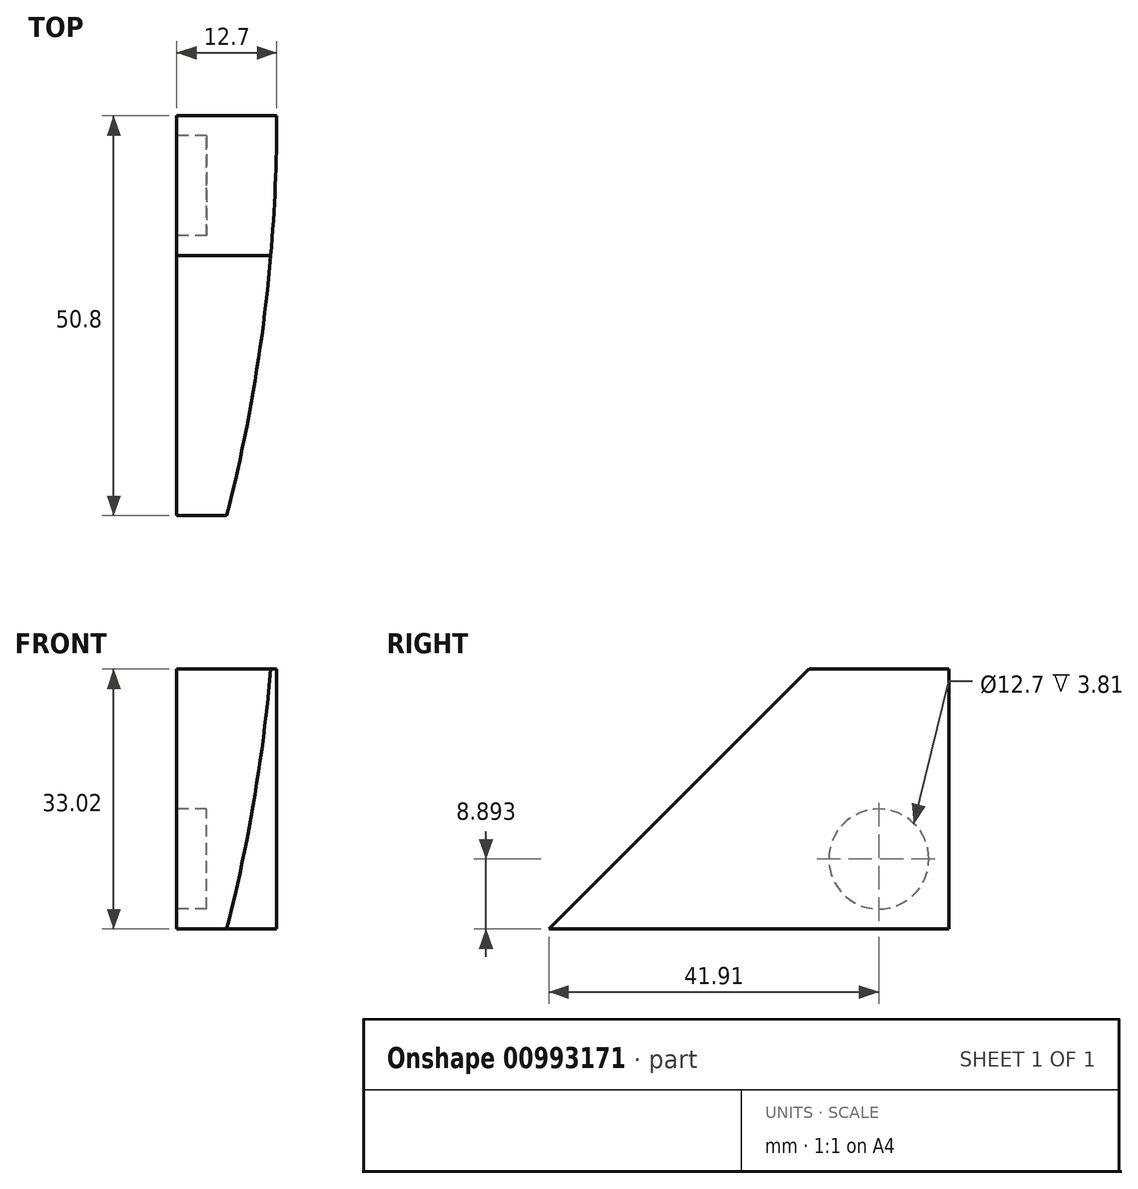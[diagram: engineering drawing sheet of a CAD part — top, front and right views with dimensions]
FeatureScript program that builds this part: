
annotation { "Feature Type Name" : "Feature", "Feature Type Description" : "" }
export const myFeature = defineFeature(function(context is Context, id is Id, definition is map)
    precondition{}
    {
        {
            var Q0;
            Q0=qCreatedBy(makeId("Right.planeOp"),FACE);
            var sketch = newSketch(context, id + "F0", { "sketchPlane" : qUnion([Q0])});
            skCircle(sketch, "E0", {"center": v(-28.5, 29.87) * mm, "radius": 6.35 * mm});
            skLineSegment(sketch, "E1.top", {"start": v(-70.4, 20.98) * mm, "end": v(-19.6, 20.98) * mm});
            skLineSegment(sketch, "E1.right", {"start": v(-19.6, 54) * mm, "end": v(-19.6, 20.98) * mm});
            skLineSegment(sketch, "E2", {"start": v(-70.4, 20.98) * mm, "end": v(-37.38, 54) * mm});
            skLineSegment(sketch, "E3", {"start": v(-37.38, 54) * mm, "end": v(-19.6, 54) * mm});
            skSolve(sketch);
        }
        {
            var Q0;
            Q0=makeQuery(id+"F0.imprint","IMPRINT",FACE,{"disambiguationData":[TD([[makeQuery(id+"F0.imprint","IMPRINT",EDGE,{"derivedFrom":sQuery(id+"F0.wireOp",EDGE,"E0")}),-1.0]])]});
            var Q1;
            Q1=makeQuery(id+"F0.imprint","IMPRINT",FACE,{"disambiguationData":[TD([[makeQuery(id+"F0.imprint","IMPRINT",EDGE,{"derivedFrom":sQuery(id+"F0.wireOp",EDGE,"E0")}),1.0]])]});
            extrude(context, id + "F1", {"entities" : qUnion([Q0, Q1]), "depth" : 12.7 * mm, "offsetDistance" : 25.4 * mm});
        }
        {
            var Q0;
            Q0=makeQuery(id+"F0.imprint","IMPRINT",FACE,{"disambiguationData":[TD([[makeQuery(id+"F0.imprint","IMPRINT",EDGE,{"derivedFrom":sQuery(id+"F0.wireOp",EDGE,"E0")}),1.0]])]});
            extrude(context, id + "F2", {"entities" : qUnion([Q0]), "operationType" : NewBodyOperationType.REMOVE, "depth" : 3.8 * mm, "offsetDistance" : 25.4 * mm});
        }
        {
            var Q0;
            Q0=makeQuery(id+"F1.opExtrude","SWEPT_FACE",FACE,{"disambiguationData":[OSD([sQuery(id+"F0.wireOp",EDGE,"E1.top")])]});
            var sketch = newSketch(context, id + "F3", { "sketchPlane" : qUnion([Q0])});
            skArc(sketch, "E4", {"start": v(12.7, 19.6) * mm, "mid": v(11.1, 45.2) * mm, "end": v(6.35, 70.4) * mm});
            skSolve(sketch);
        }
        {
            var Q0;
            {var subQ0=sQuery(id+"F3.wireOp",EDGE,"E4");Q0=makeQuery(id+"F3.imprint","IMPRINT",FACE,{"disambiguationData":[TD([[makeQuery(id+"F3.imprint","IMPRINT",EDGE,{"derivedFrom":subQ0}),-1.0]])]});}
            extrude(context, id + "F4", {"entities" : qUnion([Q0]), "operationType" : NewBodyOperationType.REMOVE, "oppositeDirection" : true, "depth" : 50.8 * mm, "offsetDistance" : 25.4 * mm});
        }
    });
